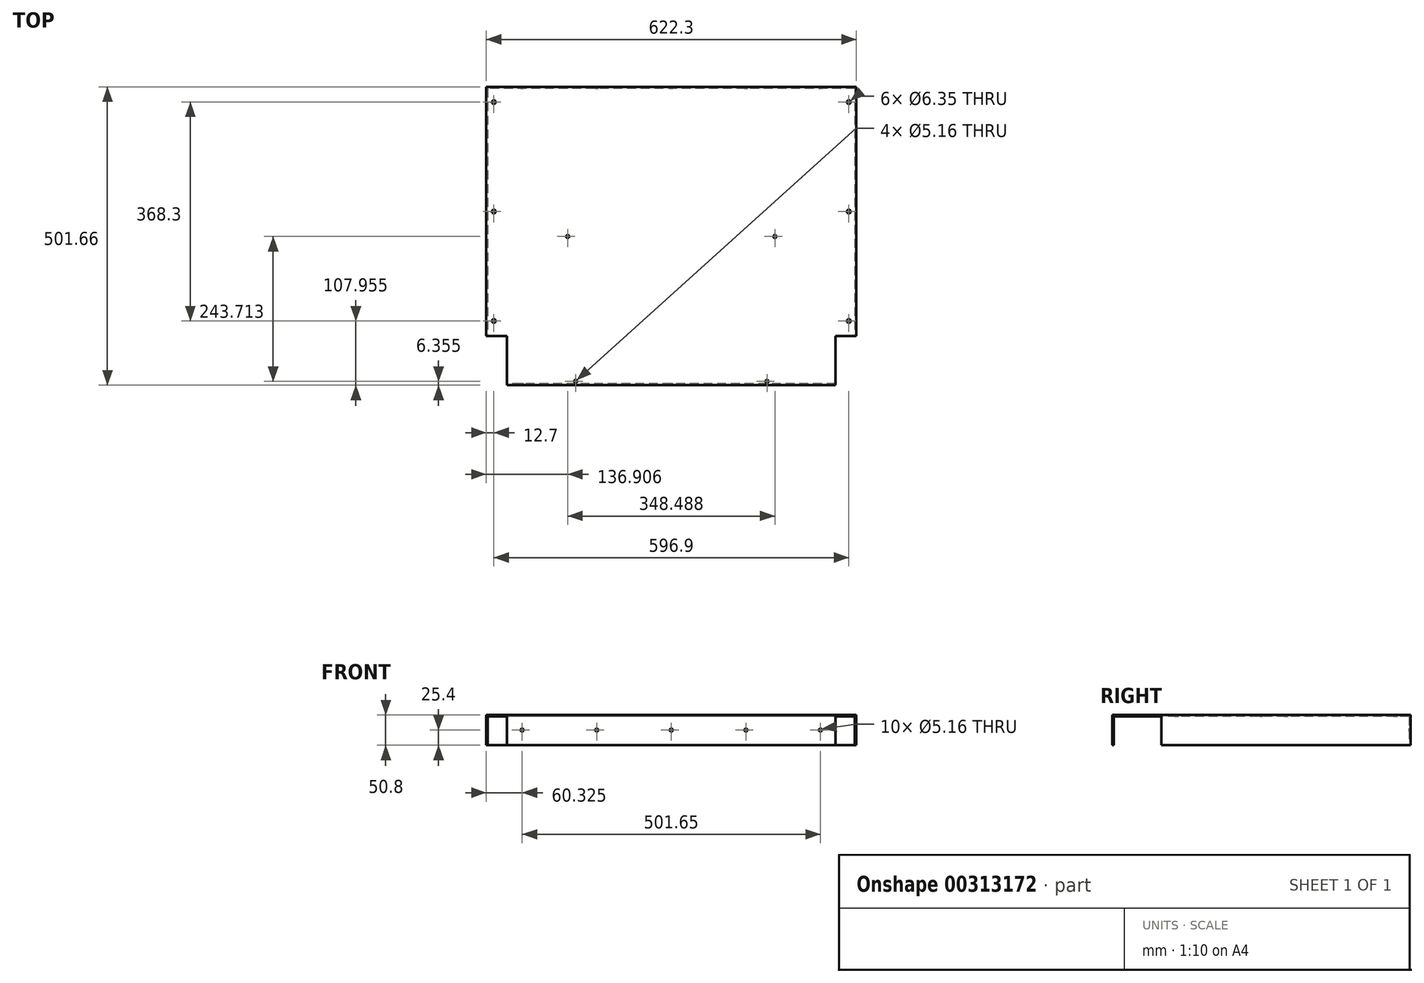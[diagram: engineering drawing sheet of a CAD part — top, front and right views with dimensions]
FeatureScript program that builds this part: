
annotation { "Feature Type Name" : "Feature", "Feature Type Description" : "" }
export const myFeature = defineFeature(function(context is Context, id is Id, definition is map)
    precondition{}
    {
        {
            var Q0;
            Q0=qCreatedBy(makeId("Top.planeOp"),FACE);
            var sketch = newSketch(context, id + "F0", { "sketchPlane" : qUnion([Q0])});
            skLineSegment(sketch, "E0.bottom", {"start": v(311.15, 250.83) * mm, "end": v(-311.15, 250.83) * mm});
            skLineSegment(sketch, "E0.top", {"start": v(311.15, -250.83) * mm, "end": v(-311.15, -250.83) * mm});
            skLineSegment(sketch, "E0.left", {"start": v(311.15, 250.83) * mm, "end": v(311.15, -250.83) * mm});
            skLineSegment(sketch, "E0.right", {"start": v(-311.15, 250.83) * mm, "end": v(-311.15, -250.83) * mm});
            skPoint(sketch, "E0.middle", {"position": v(0, 0) * mm});
            skSolve(sketch);
        }
        {
            var Q0;
            Q0=makeQuery(id+"F0.imprint","IMPRINT",FACE,{"disambiguationData":[TD([[makeQuery(id+"F0.imprint","IMPRINT",EDGE,{"derivedFrom":sQuery(id+"F0.wireOp",EDGE,"E0.bottom")}),1.0]])]});
            extrude(context, id + "F1", {"entities" : qUnion([Q0]), "endBound" : BoundingType.SYMMETRIC, "depth" : 50.8 * mm});
        }
        {
            var Q0;
            Q0=makeQuery(id+"F1.opExtrude","CAP_FACE",FACE,{"disambiguationData":[OSD([sQuery(id+"F0.wireOp",EDGE,"E0.bottom"),sQuery(id+"F0.wireOp",EDGE,"E0.top"),sQuery(id+"F0.wireOp",EDGE,"E0.left"),sQuery(id+"F0.wireOp",EDGE,"E0.right")])],"isStart":true});
            shell(context, id + "F2", {"entities" : qUnion([Q0]), "thickness" : 2.54 * mm});
        }
        {
            var Q0;
            Q0=makeQuery(id+"F1.opExtrude","CAP_FACE",FACE,{"disambiguationData":[OSD([sQuery(id+"F0.wireOp",EDGE,"E0.bottom"),sQuery(id+"F0.wireOp",EDGE,"E0.top"),sQuery(id+"F0.wireOp",EDGE,"E0.left"),sQuery(id+"F0.wireOp",EDGE,"E0.right")])],"isStart":false});
            var sketch = newSketch(context, id + "F3", { "sketchPlane" : qUnion([Q0])});
            skLineSegment(sketch, "E1.bottom", {"start": v(-311.15, -250.83) * mm, "end": v(-276.23, -250.83) * mm});
            skLineSegment(sketch, "E1.top", {"start": v(-311.15, -168.28) * mm, "end": v(-276.23, -168.28) * mm});
            skLineSegment(sketch, "E1.left", {"start": v(-311.15, -250.83) * mm, "end": v(-311.15, -168.28) * mm});
            skLineSegment(sketch, "E1.right", {"start": v(-276.23, -250.83) * mm, "end": v(-276.23, -168.28) * mm});
            skLineSegment(sketch, "E2.bottom", {"start": v(311.15, -250.83) * mm, "end": v(276.22, -250.83) * mm});
            skLineSegment(sketch, "E2.top", {"start": v(311.15, -168.28) * mm, "end": v(276.22, -168.28) * mm});
            skLineSegment(sketch, "E2.left", {"start": v(311.15, -250.83) * mm, "end": v(311.15, -168.28) * mm});
            skLineSegment(sketch, "E2.right", {"start": v(276.23, -250.83) * mm, "end": v(276.23, -168.28) * mm});
            skLineSegment(sketch, "E3.bottom", {"start": v(156.46, -241.3) * mm, "end": v(165.35, -241.3) * mm, "construction": true});
            skLineSegment(sketch, "E3.top", {"start": v(156.46, -260.35) * mm, "end": v(165.35, -260.35) * mm, "construction": true});
            skLineSegment(sketch, "E3.left", {"start": v(156.46, -241.3) * mm, "end": v(156.46, -260.35) * mm, "construction": true});
            skLineSegment(sketch, "E3.right", {"start": v(165.35, -241.3) * mm, "end": v(165.35, -260.35) * mm, "construction": true});
            skLineSegment(sketch, "E4.bottom", {"start": v(-156.46, -241.3) * mm, "end": v(-165.35, -241.3) * mm, "construction": true});
            skLineSegment(sketch, "E4.top", {"start": v(-156.46, -260.35) * mm, "end": v(-165.35, -260.35) * mm, "construction": true});
            skLineSegment(sketch, "E4.left", {"start": v(-156.46, -241.3) * mm, "end": v(-156.46, -260.35) * mm, "construction": true});
            skLineSegment(sketch, "E4.right", {"start": v(-165.35, -241.3) * mm, "end": v(-165.35, -260.35) * mm, "construction": true});
            skCircle(sketch, "E5", {"center": v(174.24, -0.76) * mm, "radius": 2.58 * mm});
            skCircle(sketch, "E6", {"center": v(-174.24, -0.76) * mm, "radius": 2.58 * mm});
            skLineSegment(sketch, "E7", {"start": v(-156.46, -241.3) * mm, "end": v(156.46, -241.3) * mm, "construction": true});
            skLineSegment(sketch, "E8", {"start": v(-174.24, -0.76) * mm, "end": v(174.24, -0.76) * mm, "construction": true});
            skLineSegment(sketch, "E9", {"start": v(0, -0.76) * mm, "end": v(0, -241.3) * mm, "construction": true});
            skCircle(sketch, "E10", {"center": v(-160.9, -244.48) * mm, "radius": 2.58 * mm});
            skPoint(sketch, "E10.centerSnap0", {"position": v(-160.9, -241.3) * mm});
            skCircle(sketch, "E11", {"center": v(160.9, -244.48) * mm, "radius": 2.58 * mm});
            skPoint(sketch, "E11.centerSnap0", {"position": v(160.9, -241.3) * mm});
            skPoint(sketch, "E11.perimeterSnap0", {"position": v(160.9, -241.3) * mm});
            skPoint(sketch, "E11.perimeterSnap1", {"position": v(-165.35, -250.83) * mm});
            skCircle(sketch, "E12", {"center": v(-298.45, 225.43) * mm, "radius": 3.18 * mm});
            skCircle(sketch, "E13", {"center": v(-298.45, 41.28) * mm, "radius": 3.18 * mm});
            skCircle(sketch, "E14", {"center": v(-298.45, -142.88) * mm, "radius": 3.18 * mm});
            skCircle(sketch, "E15", {"center": v(298.45, -142.88) * mm, "radius": 3.18 * mm});
            skCircle(sketch, "E16", {"center": v(298.45, 41.28) * mm, "radius": 3.18 * mm});
            skCircle(sketch, "E17", {"center": v(298.45, 225.43) * mm, "radius": 3.18 * mm});
            skLineSegment(sketch, "E18", {"start": v(-298.45, 225.43) * mm, "end": v(-298.45, -142.88) * mm, "construction": true});
            skSolve(sketch);
        }
        {
            var Q0;
            Q0 = qSketchRegion(id + "F3", true);
            extrude(context, id + "F4", {"entities" : qUnion([Q0]), "operationType" : NewBodyOperationType.REMOVE, "endBound" : BoundingType.THROUGH_ALL, "oppositeDirection" : true, "depth" : 25.4 * mm});
        }
        {
            var Q0;
            Q0=makeQuery(id+"F1.opExtrude","SWEPT_FACE",FACE,{"disambiguationData":[OSD([sQuery(id+"F0.wireOp",EDGE,"E0.top")])]});
            var sketch = newSketch(context, id + "F5", { "sketchPlane" : qUnion([Q0])});
            skCircle(sketch, "E19", {"center": v(0, 0) * mm, "radius": 2.58 * mm});
            skPoint(sketch, "E19.centerSnap0", {"position": v(0, 25.4) * mm});
            skPoint(sketch, "E19.centerSnap1", {"position": v(-276.23, 0) * mm});
            skCircle(sketch, "E20", {"center": v(125.41, 0) * mm, "radius": 2.58 * mm});
            skCircle(sketch, "E21", {"center": v(250.83, 0) * mm, "radius": 2.58 * mm});
            skCircle(sketch, "E22", {"center": v(-125.41, 0) * mm, "radius": 2.58 * mm});
            skCircle(sketch, "E23", {"center": v(-250.83, 0) * mm, "radius": 2.58 * mm});
            skLineSegment(sketch, "E24", {"start": v(-250.83, 0) * mm, "end": v(0, 0) * mm, "construction": true});
            skLineSegment(sketch, "E25", {"start": v(0, 0) * mm, "end": v(250.83, 0) * mm, "construction": true});
            skSolve(sketch);
        }
        {
            var Q0;
            Q0 = qSketchRegion(id + "F5", true);
            extrude(context, id + "F6", {"entities" : qUnion([Q0]), "operationType" : NewBodyOperationType.REMOVE, "endBound" : BoundingType.THROUGH_ALL, "oppositeDirection" : true, "depth" : 25.4 * mm});
        }
    });
